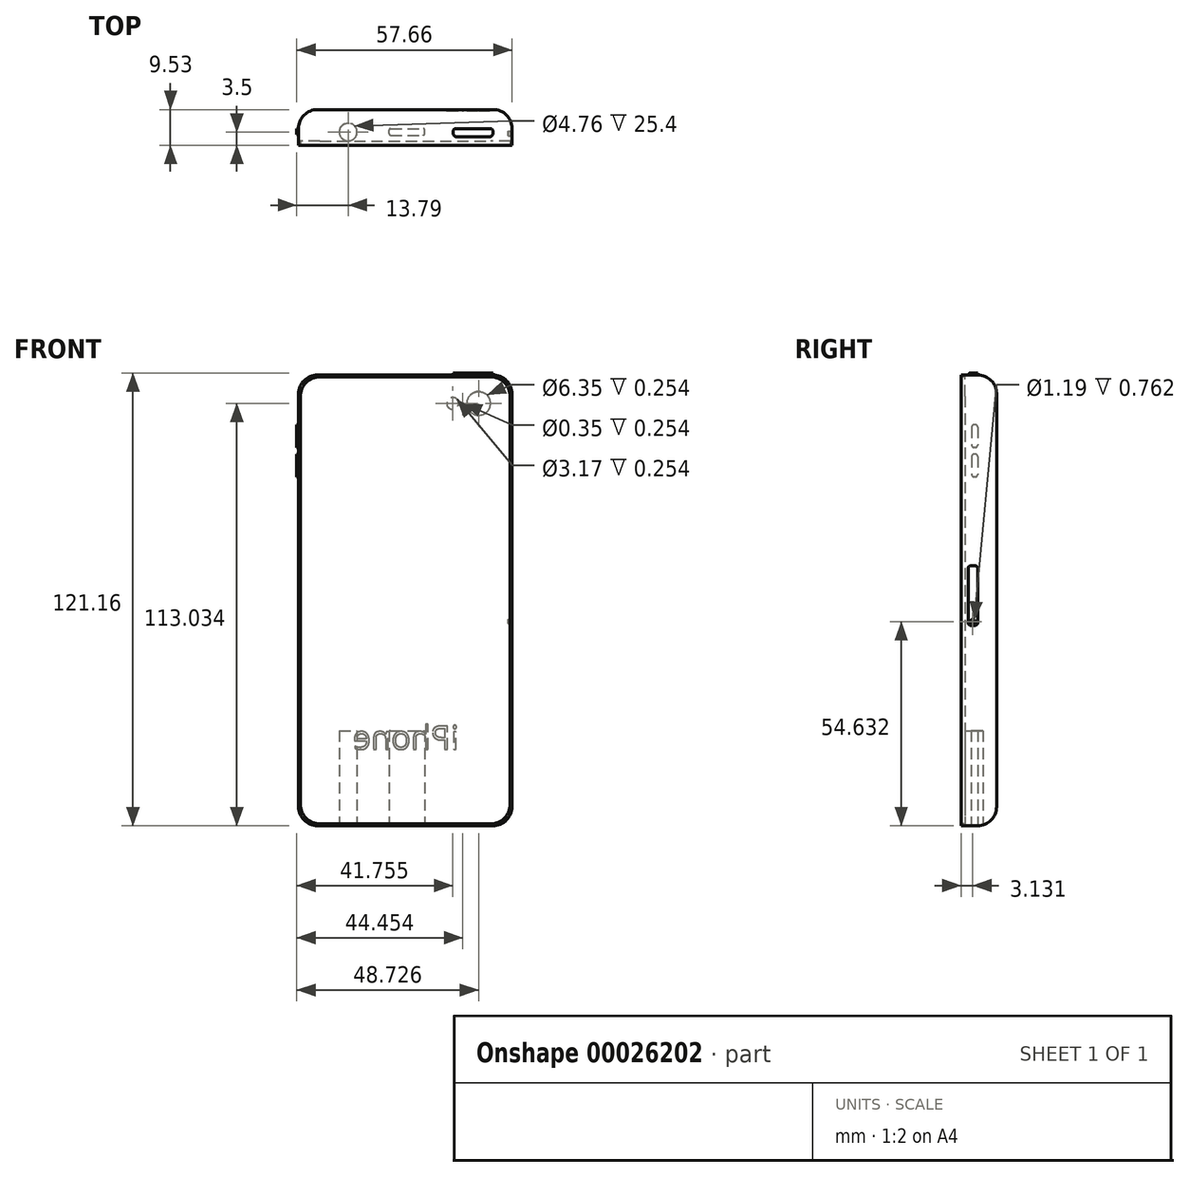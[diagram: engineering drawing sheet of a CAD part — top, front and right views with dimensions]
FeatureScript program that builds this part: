
annotation { "Feature Type Name" : "Feature", "Feature Type Description" : "" }
export const myFeature = defineFeature(function(context is Context, id is Id, definition is map)
    precondition{}
    {
        {
            var Q0;
            Q0=qCreatedBy(makeId("Front.planeOp"),FACE);
            var sketch = newSketch(context, id + "F0", { "sketchPlane" : qUnion([Q0])});
            skLineSegment(sketch, "E0.bottom", {"start": v(-30.86, 57.23) * mm, "end": v(26.3, 57.23) * mm});
            skLineSegment(sketch, "E0.top", {"start": v(-30.86, -63.42) * mm, "end": v(26.3, -63.42) * mm});
            skLineSegment(sketch, "E0.left", {"start": v(-30.86, 57.23) * mm, "end": v(-30.86, -63.42) * mm});
            skLineSegment(sketch, "E0.right", {"start": v(26.3, 57.23) * mm, "end": v(26.3, -63.42) * mm});
            skSolve(sketch);
        }
        {
            var Q0;
            Q0 = qSketchRegion(id + "F0", true);
            extrude(context, id + "F1", {"entities" : qUnion([Q0]), "depth" : 9.52 * mm});
        }
        {
            var Q0;
            Q0=makeQuery(id+"F1.opExtrude","SWEPT_EDGE",EDGE,{"disambiguationData":[OSD([sQuery(id+"F0.wireOp",EDGE,"E0.bottom"),sQuery(id+"F0.wireOp",EDGE,"E0.left")])]});
            var Q1;
            Q1=makeQuery(id+"F1.opExtrude","SWEPT_EDGE",EDGE,{"disambiguationData":[OSD([sQuery(id+"F0.wireOp",EDGE,"E0.bottom"),sQuery(id+"F0.wireOp",EDGE,"E0.right")])]});
            var Q2;
            Q2=makeQuery(id+"F1.opExtrude","SWEPT_EDGE",EDGE,{"disambiguationData":[OSD([sQuery(id+"F0.wireOp",EDGE,"E0.top"),sQuery(id+"F0.wireOp",EDGE,"E0.left")])]});
            var Q3;
            Q3=makeQuery(id+"F1.opExtrude","SWEPT_EDGE",EDGE,{"disambiguationData":[OSD([sQuery(id+"F0.wireOp",EDGE,"E0.top"),sQuery(id+"F0.wireOp",EDGE,"E0.right")])]});
            fillet(context, id + "F2", {"entities" : qUnion([Q0, Q1, Q2, Q3]), "radius" : 5.08 * mm, "tangentPropagation" : true, "allowEdgeOverflow" : false});
        }
        {
            var Q0;
            Q0=makeQuery(id+"F1.opExtrude","CAP_EDGE",EDGE,{"disambiguationData":[OSD([sQuery(id+"F0.wireOp",EDGE,"E0.left")])],"isStart":true});
            fillet(context, id + "F3", {"entities" : qUnion([Q0]), "radius" : 5.08 * mm, "tangentPropagation" : true, "allowEdgeOverflow" : false});
        }
        {
            var Q0;
            Q0=makeQuery(id+"F1.opExtrude","SWEPT_FACE",FACE,{"disambiguationData":[OSD([sQuery(id+"F0.wireOp",EDGE,"E0.top")])]});
            var sketch = newSketch(context, id + "F4", { "sketchPlane" : qUnion([Q0])});
            skCircle(sketch, "E1", {"center": v(-17.58, 6.03) * mm, "radius": 2.38 * mm});
            skSolve(sketch);
        }
        {
            var Q0;
            {var subQ0=sQuery(id+"F0.wireOp",EDGE,"E0.top");var subQ1=makeQuery(id+"F3.opFillet","BLEND_EDGE",EDGE,{"blendedFrom":[makeQuery(id+"F1.opExtrude","CAP_EDGE",EDGE,{"disambiguationData":[OSD([subQ0])],"isStart":true}),makeQuery(id+"F1.opExtrude","SWEPT_FACE",FACE,{"disambiguationData":[OSD([subQ0])]})],"blendedInto":[makeQuery(id+"F1.opExtrude","SWEPT_FACE",FACE,{"disambiguationData":[OSD([subQ0])]})]});var subQ2=sQuery(id+"F4.wireOp",EDGE,"E1");var subQ4=makeQuery(id+"F4.imprint","INTERSECT",VERTEX,{"disambiguationData":[OD(0.0)],"derivedFrom":[subQ1,subQ2]});Q0=makeQuery(id+"F4.imprint","IMPRINT",FACE,{"disambiguationData":[TD([[makeQuery(id+"F4.imprint","IMPRINT",EDGE,{"disambiguationData":[TD([[subQ4,1.0]])],"derivedFrom":subQ2}),1.0]])]});}
            var Q1;
            {var subQ0=sQuery(id+"F0.wireOp",EDGE,"E0.top");var subQ1=makeQuery(id+"F3.opFillet","BLEND_EDGE",EDGE,{"blendedFrom":[makeQuery(id+"F1.opExtrude","CAP_EDGE",EDGE,{"disambiguationData":[OSD([subQ0])],"isStart":true}),makeQuery(id+"F1.opExtrude","SWEPT_FACE",FACE,{"disambiguationData":[OSD([subQ0])]})],"blendedInto":[makeQuery(id+"F1.opExtrude","SWEPT_FACE",FACE,{"disambiguationData":[OSD([subQ0])]})]});var subQ2=sQuery(id+"F4.wireOp",EDGE,"E1");var subQ4=makeQuery(id+"F4.imprint","INTERSECT",VERTEX,{"disambiguationData":[OD(0.0)],"derivedFrom":[subQ1,subQ2]});Q1=makeQuery(id+"F4.imprint","IMPRINT",FACE,{"disambiguationData":[TD([[makeQuery(id+"F4.imprint","IMPRINT",EDGE,{"disambiguationData":[TD([[subQ4,-1.0]])],"derivedFrom":subQ2}),1.0]])]});}
            extrude(context, id + "F5", {"entities" : qUnion([Q0, Q1]), "operationType" : NewBodyOperationType.REMOVE, "oppositeDirection" : true, "depth" : 25.4 * mm});
        }
        {
            var Q0;
            Q0=makeQuery(id+"F1.opExtrude","SWEPT_FACE",FACE,{"disambiguationData":[OSD([sQuery(id+"F0.wireOp",EDGE,"E0.top")])]});
            var sketch = newSketch(context, id + "F6", { "sketchPlane" : qUnion([Q0])});
            skLineSegment(sketch, "E2.bottom", {"start": v(-6.21, 6.86) * mm, "end": v(2.5, 6.86) * mm});
            skLineSegment(sketch, "E2.top", {"start": v(-6.21, 5.08) * mm, "end": v(2.5, 5.08) * mm});
            skLineSegment(sketch, "E2.left", {"start": v(-6.62, 6.46) * mm, "end": v(-6.62, 5.48) * mm});
            skLineSegment(sketch, "E2.right", {"start": v(2.9, 6.46) * mm, "end": v(2.9, 5.48) * mm});
            skPoint(sketch, "E3.visualSharp", {"position": v(-6.62, 6.86) * mm});
            skArc(sketch, "E3.filletArc", {"start": v(-6.21, 6.86) * mm, "mid": v(-6.5, 6.74) * mm, "end": v(-6.62, 6.46) * mm});
            skPoint(sketch, "E4.visualSharp", {"position": v(2.9, 5.08) * mm});
            skArc(sketch, "E4.filletArc", {"start": v(2.5, 5.08) * mm, "mid": v(2.8, 5.2) * mm, "end": v(2.9, 5.48) * mm});
            skPoint(sketch, "E5.visualSharp", {"position": v(2.9, 6.86) * mm});
            skArc(sketch, "E5.filletArc", {"start": v(2.9, 6.46) * mm, "mid": v(2.8, 6.74) * mm, "end": v(2.5, 6.86) * mm});
            skPoint(sketch, "E6.visualSharp", {"position": v(-6.62, 5.08) * mm});
            skArc(sketch, "E6.filletArc", {"start": v(-6.62, 5.48) * mm, "mid": v(-6.5, 5.2) * mm, "end": v(-6.21, 5.08) * mm});
            skSolve(sketch);
        }
        {
            var Q0;
            Q0=makeQuery(id+"F6.imprint","IMPRINT",FACE,{"disambiguationData":[TD([[makeQuery(id+"F6.imprint","IMPRINT",EDGE,{"derivedFrom":sQuery(id+"F6.wireOp",EDGE,"E2.bottom")}),-1.0]])]});
            extrude(context, id + "F7", {"entities" : qUnion([Q0]), "operationType" : NewBodyOperationType.REMOVE, "oppositeDirection" : true, "depth" : 25.4 * mm});
        }
        {
            var Q0;
            Q0=makeQuery(id+"F1.opExtrude","CAP_FACE",FACE,{"disambiguationData":[OSD([sQuery(id+"F0.wireOp",EDGE,"E0.bottom"),sQuery(id+"F0.wireOp",EDGE,"E0.top"),sQuery(id+"F0.wireOp",EDGE,"E0.left"),sQuery(id+"F0.wireOp",EDGE,"E0.right")])],"isStart":false});
            var sketch = newSketch(context, id + "F8", { "sketchPlane" : qUnion([Q0])});
            skLineSegment(sketch, "E7.0", {"start": v(-25.16, 56.73) * mm, "end": v(20.6, 56.73) * mm});
            skLineSegment(sketch, "E8.0", {"start": v(-30.35, 51.54) * mm, "end": v(-30.35, -57.72) * mm});
            skLineSegment(sketch, "E9.0", {"start": v(25.78, 51.54) * mm, "end": v(25.78, -57.72) * mm});
            skLineSegment(sketch, "E10.0", {"start": v(-25.16, -62.9) * mm, "end": v(20.6, -62.9) * mm});
            skArc(sketch, "E11.filletArc", {"start": v(-25.16, 56.73) * mm, "mid": v(-28.83, 55.2) * mm, "end": v(-30.35, 51.54) * mm});
            skArc(sketch, "E12.filletArc", {"start": v(25.78, 51.54) * mm, "mid": v(24.26, 55.2) * mm, "end": v(20.6, 56.73) * mm});
            skArc(sketch, "E13.filletArc", {"start": v(20.6, -62.9) * mm, "mid": v(24.26, -61.39) * mm, "end": v(25.78, -57.72) * mm});
            skArc(sketch, "E14.filletArc", {"start": v(-30.35, -57.72) * mm, "mid": v(-28.83, -61.39) * mm, "end": v(-25.16, -62.9) * mm});
            skSolve(sketch);
        }
        {
            var Q0;
            Q0 = qSketchRegion(id + "F8", true);
            extrude(context, id + "F9", {"entities" : qUnion([Q0]), "operationType" : NewBodyOperationType.REMOVE, "oppositeDirection" : true, "depth" : 1.06 * mm});
        }
        {
            var Q0;
            Q0=makeQuery(id+"F1.opExtrude","SWEPT_FACE",FACE,{"disambiguationData":[OSD([sQuery(id+"F0.wireOp",EDGE,"E0.bottom")])]});
            var sketch = newSketch(context, id + "F10", { "sketchPlane" : qUnion([Q0])});
            skLineSegment(sketch, "E15.bottom", {"start": v(20.2, -7.3) * mm, "end": v(11.51, -7.3) * mm});
            skLineSegment(sketch, "E15.top", {"start": v(20.38, -5.08) * mm, "end": v(11.33, -5.08) * mm});
            skLineSegment(sketch, "E15.left", {"start": v(21.21, -6.29) * mm, "end": v(21.21, -5.91) * mm});
            skLineSegment(sketch, "E15.right", {"start": v(10.5, -6.29) * mm, "end": v(10.5, -5.91) * mm});
            skPoint(sketch, "E16.visualSharp", {"position": v(21.21, -7.3) * mm});
            skArc(sketch, "E16.filletArc", {"start": v(20.2, -7.3) * mm, "mid": v(20.92, -7) * mm, "end": v(21.21, -6.29) * mm});
            skPoint(sketch, "E17.visualSharp", {"position": v(10.5, -7.3) * mm});
            skArc(sketch, "E17.filletArc", {"start": v(10.5, -6.29) * mm, "mid": v(10.8, -7) * mm, "end": v(11.51, -7.3) * mm});
            skPoint(sketch, "E18.visualSharp", {"position": v(21.21, -5.08) * mm});
            skArc(sketch, "E18.filletArc", {"start": v(21.21, -5.91) * mm, "mid": v(20.97, -5.32) * mm, "end": v(20.38, -5.08) * mm});
            skPoint(sketch, "E19.visualSharp", {"position": v(10.5, -5.08) * mm});
            skArc(sketch, "E19.filletArc", {"start": v(11.33, -5.08) * mm, "mid": v(10.74, -5.32) * mm, "end": v(10.5, -5.91) * mm});
            skSolve(sketch);
        }
        {
            var Q0;
            Q0=makeQuery(id+"F10.imprint","IMPRINT",FACE,{"disambiguationData":[TD([[makeQuery(id+"F10.imprint","IMPRINT",EDGE,{"derivedFrom":sQuery(id+"F10.wireOp",EDGE,"E15.bottom")}),-1.0]])]});
            extrude(context, id + "F11", {"entities" : qUnion([Q0]), "operationType" : NewBodyOperationType.ADD, "depth" : 0.5 * mm});
        }
        {
            var Q0;
            Q0=makeQuery(id+"F1.opExtrude","SWEPT_FACE",FACE,{"disambiguationData":[OSD([sQuery(id+"F0.wireOp",EDGE,"E0.left")])]});
            var sketch = newSketch(context, id + "F12", { "sketchPlane" : qUnion([Q0])});
            skLineSegment(sketch, "E20.bottom", {"start": v(5.08, 49.93) * mm, "end": v(6.67, 49.93) * mm});
            skLineSegment(sketch, "E20.top", {"start": v(5.33, 45.6) * mm, "end": v(6.67, 45.6) * mm});
            skLineSegment(sketch, "E20.left", {"start": v(5.08, 49.68) * mm, "end": v(5.08, 45.85) * mm});
            skLineSegment(sketch, "E20.right", {"start": v(6.67, 49.93) * mm, "end": v(6.67, 45.6) * mm});
            skLineSegment(sketch, "E21.bottom", {"start": v(5.72, 43.92) * mm, "end": v(6.03, 43.92) * mm});
            skLineSegment(sketch, "E21.top", {"start": v(5.72, 37.82) * mm, "end": v(6.03, 37.82) * mm});
            skLineSegment(sketch, "E21.left", {"start": v(5.08, 43.28) * mm, "end": v(5.08, 38.45) * mm});
            skLineSegment(sketch, "E21.right", {"start": v(6.67, 43.28) * mm, "end": v(6.67, 38.45) * mm});
            skLineSegment(sketch, "E22.bottom", {"start": v(5.72, 36.04) * mm, "end": v(6.03, 36.04) * mm});
            skLineSegment(sketch, "E22.top", {"start": v(5.72, 29.95) * mm, "end": v(6.03, 29.95) * mm});
            skLineSegment(sketch, "E22.left", {"start": v(5.08, 35.4) * mm, "end": v(5.08, 30.58) * mm});
            skLineSegment(sketch, "E22.right", {"start": v(6.67, 35.4) * mm, "end": v(6.67, 30.58) * mm});
            skLineSegment(sketch, "E23.bottom", {"start": v(5.33, 49.93) * mm, "end": v(5.62, 49.93) * mm});
            skLineSegment(sketch, "E23.top", {"start": v(5.08, 45.6) * mm, "end": v(5.62, 45.6) * mm});
            skLineSegment(sketch, "E23.left", {"start": v(5.08, 49.93) * mm, "end": v(5.08, 45.6) * mm});
            skLineSegment(sketch, "E23.right", {"start": v(5.87, 49.68) * mm, "end": v(5.87, 45.85) * mm});
            skPoint(sketch, "E24.visualSharp", {"position": v(5.08, 43.92) * mm});
            skArc(sketch, "E24.filletArc", {"start": v(5.72, 43.92) * mm, "mid": v(5.27, 43.73) * mm, "end": v(5.08, 43.28) * mm});
            skPoint(sketch, "E25.visualSharp", {"position": v(6.67, 43.92) * mm});
            skArc(sketch, "E25.filletArc", {"start": v(6.67, 43.28) * mm, "mid": v(6.48, 43.73) * mm, "end": v(6.03, 43.92) * mm});
            skPoint(sketch, "E26.visualSharp", {"position": v(5.08, 37.82) * mm});
            skArc(sketch, "E26.filletArc", {"start": v(5.08, 38.45) * mm, "mid": v(5.27, 38) * mm, "end": v(5.72, 37.82) * mm});
            skPoint(sketch, "E27.visualSharp", {"position": v(6.67, 37.82) * mm});
            skArc(sketch, "E27.filletArc", {"start": v(6.03, 37.82) * mm, "mid": v(6.48, 38) * mm, "end": v(6.67, 38.45) * mm});
            skPoint(sketch, "E28.visualSharp", {"position": v(5.08, 36.04) * mm});
            skArc(sketch, "E28.filletArc", {"start": v(5.72, 36.04) * mm, "mid": v(5.27, 35.86) * mm, "end": v(5.08, 35.4) * mm});
            skPoint(sketch, "E29.visualSharp", {"position": v(6.67, 36.04) * mm});
            skArc(sketch, "E29.filletArc", {"start": v(6.67, 35.4) * mm, "mid": v(6.48, 35.86) * mm, "end": v(6.03, 36.04) * mm});
            skPoint(sketch, "E30.visualSharp", {"position": v(5.08, 29.95) * mm});
            skArc(sketch, "E30.filletArc", {"start": v(5.08, 30.58) * mm, "mid": v(5.27, 30.13) * mm, "end": v(5.72, 29.95) * mm});
            skPoint(sketch, "E31.visualSharp", {"position": v(6.67, 29.95) * mm});
            skArc(sketch, "E31.filletArc", {"start": v(6.03, 29.95) * mm, "mid": v(6.48, 30.13) * mm, "end": v(6.67, 30.58) * mm});
            skPoint(sketch, "E32.visualSharp", {"position": v(5.87, 45.6) * mm});
            skArc(sketch, "E32.filletArc", {"start": v(5.62, 45.6) * mm, "mid": v(5.8, 45.67) * mm, "end": v(5.87, 45.85) * mm});
            skPoint(sketch, "E33.visualSharp", {"position": v(5.08, 45.6) * mm});
            skArc(sketch, "E33.filletArc", {"start": v(5.08, 45.85) * mm, "mid": v(5.15, 45.67) * mm, "end": v(5.33, 45.6) * mm});
            skPoint(sketch, "E34.visualSharp", {"position": v(5.08, 49.93) * mm});
            skArc(sketch, "E34.filletArc", {"start": v(5.33, 49.93) * mm, "mid": v(5.15, 49.86) * mm, "end": v(5.08, 49.68) * mm});
            skPoint(sketch, "E35.visualSharp", {"position": v(5.87, 49.93) * mm});
            skArc(sketch, "E35.filletArc", {"start": v(5.87, 49.68) * mm, "mid": v(5.8, 49.86) * mm, "end": v(5.62, 49.93) * mm});
            skSolve(sketch);
        }
        {
            var Q0;
            Q0=makeQuery(id+"F12.imprint","IMPRINT",FACE,{"disambiguationData":[TD([[makeQuery(id+"F12.imprint","IMPRINT",EDGE,{"derivedFrom":sQuery(id+"F12.wireOp",EDGE,"E23.bottom")}),-1.0]])]});
            var Q1;
            Q1=makeQuery(id+"F12.imprint","IMPRINT",FACE,{"disambiguationData":[TD([[makeQuery(id+"F12.imprint","IMPRINT",EDGE,{"derivedFrom":sQuery(id+"F12.wireOp",EDGE,"E21.bottom")}),-1.0]])]});
            var Q2;
            Q2=makeQuery(id+"F12.imprint","IMPRINT",FACE,{"disambiguationData":[TD([[makeQuery(id+"F12.imprint","IMPRINT",EDGE,{"derivedFrom":sQuery(id+"F12.wireOp",EDGE,"E22.bottom")}),-1.0]])]});
            extrude(context, id + "F13", {"entities" : qUnion([Q0, Q1, Q2]), "operationType" : NewBodyOperationType.ADD, "depth" : 0.5 * mm});
        }
        {
            var Q0;
            Q0=makeQuery(id+"F1.opExtrude","CAP_FACE",FACE,{"disambiguationData":[OSD([sQuery(id+"F0.wireOp",EDGE,"E0.bottom"),sQuery(id+"F0.wireOp",EDGE,"E0.top"),sQuery(id+"F0.wireOp",EDGE,"E0.left"),sQuery(id+"F0.wireOp",EDGE,"E0.right")])],"isStart":true});
            var sketch = newSketch(context, id + "F14", { "sketchPlane" : qUnion([Q0])});
            skLineSegment(sketch, "E36.0", {"start": v(25.78, 49.61) * mm, "end": v(-21.21, 49.61) * mm});
            skCircle(sketch, "E37", {"center": v(-17.36, 49.61) * mm, "radius": 3.18 * mm});
            skCircle(sketch, "E38", {"center": v(-10.39, 49.61) * mm, "radius": 1.59 * mm});
            skCircle(sketch, "E39", {"center": v(-13.08, 49.61) * mm, "radius": 0.17 * mm});
            skSolve(sketch);
        }
        {
            var Q0;
            Q0 = qSketchRegion(id + "F14", true);
            extrude(context, id + "F15", {"entities" : qUnion([Q0]), "operationType" : NewBodyOperationType.REMOVE, "oppositeDirection" : true, "depth" : 0.25 * mm});
        }
        {
            var Q0;
            Q0=makeQuery(id+"F1.opExtrude","SWEPT_FACE",FACE,{"disambiguationData":[OSD([sQuery(id+"F0.wireOp",EDGE,"E0.right")])]});
            var sketch = newSketch(context, id + "F16", { "sketchPlane" : qUnion([Q0])});
            skLineSegment(sketch, "E40.bottom", {"start": v(-6.99, 6.12) * mm, "end": v(-5.72, 6.12) * mm});
            skLineSegment(sketch, "E40.top", {"start": v(-6.99, -9.78) * mm, "end": v(-5.72, -9.78) * mm});
            skLineSegment(sketch, "E40.left", {"start": v(-7.62, 5.49) * mm, "end": v(-7.62, -9.15) * mm});
            skLineSegment(sketch, "E40.right", {"start": v(-5.08, 5.49) * mm, "end": v(-5.08, -9.15) * mm});
            skPoint(sketch, "E41.visualSharp", {"position": v(-7.62, 6.12) * mm});
            skArc(sketch, "E41.filletArc", {"start": v(-6.99, 6.12) * mm, "mid": v(-7.43, 5.94) * mm, "end": v(-7.62, 5.49) * mm});
            skPoint(sketch, "E42.visualSharp", {"position": v(-5.08, 6.12) * mm});
            skArc(sketch, "E42.filletArc", {"start": v(-5.08, 5.49) * mm, "mid": v(-5.27, 5.94) * mm, "end": v(-5.72, 6.12) * mm});
            skPoint(sketch, "E43.visualSharp", {"position": v(-7.62, -9.78) * mm});
            skArc(sketch, "E43.filletArc", {"start": v(-7.62, -9.15) * mm, "mid": v(-7.43, -9.6) * mm, "end": v(-6.99, -9.78) * mm});
            skPoint(sketch, "E44.visualSharp", {"position": v(-5.08, -9.78) * mm});
            skArc(sketch, "E44.filletArc", {"start": v(-5.72, -9.78) * mm, "mid": v(-5.27, -9.6) * mm, "end": v(-5.08, -9.15) * mm});
            skSolve(sketch);
        }
        {
            var Q0;
            Q0 = qSketchRegion(id + "F16", true);
            extrude(context, id + "F17", {"entities" : qUnion([Q0]), "operationType" : NewBodyOperationType.REMOVE, "oppositeDirection" : true, "depth" : 0.25 * mm});
        }
        {
            var Q0;
            Q0=makeQuery(id+"F17.boolean.opBoolean","COPY",FACE,{"derivedFrom":makeQuery(id+"F17.opExtrude","CAP_FACE",FACE,{"disambiguationData":[OSD([sQuery(id+"F16.wireOp",EDGE,"E40.bottom"),sQuery(id+"F16.wireOp",EDGE,"E40.top"),sQuery(id+"F16.wireOp",EDGE,"E40.left"),sQuery(id+"F16.wireOp",EDGE,"E40.right"),sQuery(id+"F16.wireOp",EDGE,"E41.filletArc"),sQuery(id+"F16.wireOp",EDGE,"E42.filletArc"),sQuery(id+"F16.wireOp",EDGE,"E43.filletArc"),sQuery(id+"F16.wireOp",EDGE,"E44.filletArc")])],"isStart":false})});
            var sketch = newSketch(context, id + "F18", { "sketchPlane" : qUnion([Q0])});
            skCircle(sketch, "E45", {"center": v(-6.4, -8.79) * mm, "radius": 0.6 * mm});
            skSolve(sketch);
        }
        {
            var Q0;
            Q0 = qSketchRegion(id + "F18", true);
            extrude(context, id + "F19", {"entities" : qUnion([Q0]), "operationType" : NewBodyOperationType.REMOVE, "oppositeDirection" : true, "depth" : 0.76 * mm});
        }
        {
            var Q0;
            Q0=makeQuery(id+"F1.opExtrude","CAP_FACE",FACE,{"disambiguationData":[OSD([sQuery(id+"F0.wireOp",EDGE,"E0.bottom"),sQuery(id+"F0.wireOp",EDGE,"E0.top"),sQuery(id+"F0.wireOp",EDGE,"E0.left"),sQuery(id+"F0.wireOp",EDGE,"E0.right")])],"isStart":true});
            var sketch = newSketch(context, id + "F20", { "sketchPlane" : qUnion([Q0])});
            skText(sketch, "E46", { "text": "iPhone\n", "fontName": "OpenSans-Regular.ttf"});
            const initialGuessF20  = {"E46": [-0.01208, -0.04296, 1, 0, 0.00631]};
            skSetInitialGuess(sketch, initialGuessF20);
            skSolve(sketch);
        }
        {
            var Q0;
            Q0 = qSketchRegion(id + "F20", true);
            extrude(context, id + "F21", {"entities" : qUnion([Q0]), "operationType" : NewBodyOperationType.REMOVE, "oppositeDirection" : true, "depth" : 0.03 * mm});
        }
    });
